FCSTD DOCUMENT  (FreeCAD 0.20R0.20.2)
Label: 0.003
License: All rights reserved
LicenseURL: http://en.wikipedia.org/wiki/All_rights_reserved
objects: Sketcher::SketchObject×1
note: 1 computed .brp shape members not serialized (recipe doc carries the construction recipe); baked Part::Feature solids carry a one-line shape summary decoded from their .brp

FEATURE [Sketcher::SketchObject] Sketch
  FullyConstrained = true
  sketch-geometry (37):
    g0: Circle CenterX=0 CenterY=0 CenterZ=0 NormalX=0 NormalY=0 NormalZ=1 AngleXU=0 Radius=0.9
    g1: LineSegment StartX=0 StartY=0 StartZ=0 EndX=12 EndY=0 EndZ=0
    g2: LineSegment StartX=0 StartY=0 StartZ=0 EndX=-12 EndY=0 EndZ=0
    g3: LineSegment StartX=12 StartY=0 StartZ=0 EndX=12 EndY=38 EndZ=0
    g4: LineSegment StartX=12 StartY=0 StartZ=0 EndX=12 EndY=-38 EndZ=0
    g5: LineSegment StartX=12 StartY=38 StartZ=0 EndX=9 EndY=38 EndZ=0
    g6: LineSegment StartX=12 StartY=-38 StartZ=0 EndX=9 EndY=-38 EndZ=0
    g7: LineSegment StartX=-12 StartY=0 StartZ=0 EndX=-12 EndY=6 EndZ=0
    g8: LineSegment StartX=-12 StartY=0 StartZ=0 EndX=-12 EndY=-6 EndZ=0
    g9: LineSegment StartX=-12 StartY=6 StartZ=0 EndX=-12 EndY=16 EndZ=0
    g10: LineSegment StartX=-12 StartY=-6 StartZ=0 EndX=-12 EndY=-16 EndZ=0
    g11: LineSegment StartX=-12 StartY=16 StartZ=0 EndX=6 EndY=16 EndZ=0
    g12: LineSegment StartX=-12 StartY=-16 StartZ=0 EndX=6 EndY=-16 EndZ=0
    g13: Circle CenterX=-12 CenterY=6 CenterZ=0 NormalX=0 NormalY=0 NormalZ=1 AngleXU=0 Radius=1
    g14: Circle CenterX=6 CenterY=16 CenterZ=0 NormalX=0 NormalY=0 NormalZ=1 AngleXU=0 Radius=1
    g15: Circle CenterX=9 CenterY=38 CenterZ=0 NormalX=0 NormalY=0 NormalZ=1 AngleXU=0 Radius=1
    g16: BSplineCurve PolesCount=3 KnotsCount=2 Degree=2 IsPeriodic=0
    g17: GeomPoint X=-12 Y=6 Z=0
    g18: GeomPoint X=9 Y=38 Z=0
    g19: Circle CenterX=-12 CenterY=-6 CenterZ=0 NormalX=0 NormalY=0 NormalZ=1 AngleXU=0 Radius=1
    g20: Circle CenterX=6 CenterY=-16 CenterZ=0 NormalX=0 NormalY=0 NormalZ=1 AngleXU=0 Radius=1
    g21: Circle CenterX=9 CenterY=-38 CenterZ=0 NormalX=0 NormalY=0 NormalZ=1 AngleXU=0 Radius=1
    g22: BSplineCurve PolesCount=3 KnotsCount=2 Degree=2 IsPeriodic=0
    g23: GeomPoint X=-12 Y=-6 Z=0
    g24: GeomPoint X=9 Y=-38 Z=0
    g25: LineSegment StartX=6 StartY=-16 StartZ=0 EndX=6 EndY=-12 EndZ=0
    g26: LineSegment StartX=6 StartY=16 StartZ=0 EndX=6 EndY=12 EndZ=0
    g27: Circle CenterX=6 CenterY=12 CenterZ=0 NormalX=0 NormalY=0 NormalZ=1 AngleXU=0 Radius=4
    g28: Circle CenterX=6 CenterY=-12 CenterZ=0 NormalX=0 NormalY=0 NormalZ=1 AngleXU=0 Radius=4
    g29: LineSegment StartX=6 StartY=-12 StartZ=0 EndX=9 EndY=-12 EndZ=0
    g30: LineSegment StartX=6 StartY=12 StartZ=0 EndX=9 EndY=12 EndZ=0
    g31: LineSegment StartX=9 StartY=-12 StartZ=0 EndX=9 EndY=-24 EndZ=0
    g32: LineSegment StartX=9 StartY=-24 StartZ=0 EndX=7 EndY=-24 EndZ=0
    g33: Circle CenterX=9 CenterY=-24 CenterZ=0 NormalX=0 NormalY=0 NormalZ=1 AngleXU=0 Radius=2
    g34: LineSegment StartX=9 StartY=12 StartZ=0 EndX=9 EndY=24 EndZ=0
    g35: LineSegment StartX=9 StartY=24 StartZ=0 EndX=7 EndY=24 EndZ=0
    g36: Circle CenterX=9 CenterY=24 CenterZ=0 NormalX=0 NormalY=0 NormalZ=1 AngleXU=0 Radius=2
  constraints (91):
    c: Block(g0)
    c: Coincident(g1,g0)
    c: Horizontal(g1)
    c: Distance(g1) = 12
    c: Coincident(g2,g0)
    c: Horizontal(g2)
    c: Distance(g2) = 12
    c: Coincident(g3,g1)
    c: Vertical(g3)
    c: Distance(g3) = 38
    c: Coincident(g4,g1)
    c: Vertical(g4)
    c: Distance(g4) = 38
    c: Coincident(g5,g3)
    c: Horizontal(g5)
    c: Coincident(g6,g4)
    c: Horizontal(g6)
    c: Distance(g6) = 3
    c: Distance(g5) = 3
    c: Coincident(g7,g2)
    c: Vertical(g7)
    c: Coincident(g8,g2)
    c: Vertical(g8)
    c: Distance(g7) = 6
    c: Distance(g8) = 6
    c: Coincident(g9,g7)
    c: Vertical(g9)
    c: Coincident(g10,g8)
    c: Vertical(g10)
    c: Distance(g9) = 10
    c: Distance(g10) = 10
    c: Coincident(g11,g9)
    c: Horizontal(g11)
    c: Coincident(g12,g10)
    c: Horizontal(g12)
    c: Distance(g11) = 18
    c: Distance(g12) = 18
    c: Weight(g13) = 1
    c: Coincident(g16,g7)
    c: Equal(g13,g14)
    c: Coincident(g14,g11)
    c: Equal(g13,g15)
    c: Coincident(g16,g5)
    c: InternalAlignment(g13,g16)
    c: InternalAlignment(g14,g16)
    c: InternalAlignment(g15,g16)
    c: InternalAlignment(g17,g16)
    c: InternalAlignment(g18,g16)
    c: Weight(g19) = 1
    c: Coincident(g22,g8)
    c: Equal(g19,g20)
    c: Coincident(g20,g12)
    c: Equal(g19,g21)
    c: Coincident(g22,g6)
    c: InternalAlignment(g19,g22)
    c: InternalAlignment(g20,g22)
    c: InternalAlignment(g21,g22)
    c: InternalAlignment(g23,g22)
    c: InternalAlignment(g24,g22)
    c: Coincident(g25,g12)
    c: Vertical(g25)
    c: Coincident(g26,g11)
    c: Vertical(g26)
    c: Distance(g26) = 4
    c: Distance(g25) = 4
    c: Coincident(g27,g26)
    c: PointOnObject(g11,g27)
    c: Coincident(g28,g25)
    c: PointOnObject(g12,g28)
    c: Coincident(g29,g25)
    c: Horizontal(g29)
    c: Coincident(g30,g26)
    c: Horizontal(g30)
    c: Distance(g30) = 3
    c: Distance(g29) = 3
    c: Coincident(g31,g29)
    c: Vertical(g31)
    c: Distance(g31) = 12
    c: Coincident(g32,g31)
    c: Distance(g32) = 2
    c: Horizontal(g32)
    c: Coincident(g33,g31)
    c: PointOnObject(g32,g33)
    c: Coincident(g34,g30)
    c: Vertical(g34)
    c: Distance(g34) = 12
    c: Coincident(g35,g34)
    c: Horizontal(g35)
    c: Distance(g35) = 2
    c: Coincident(g36,g34)
    c: PointOnObject(g35,g36)
